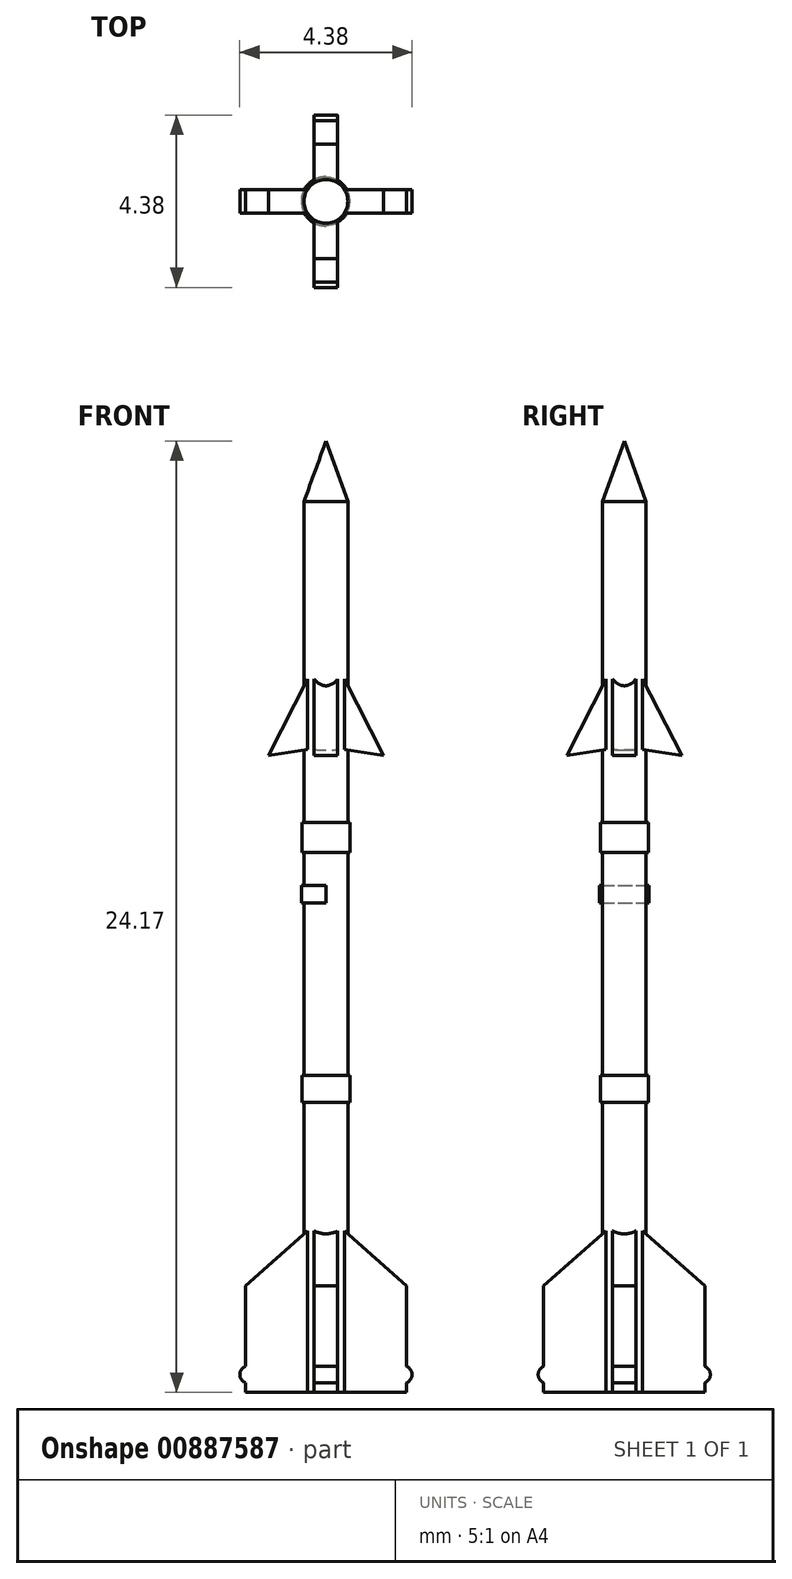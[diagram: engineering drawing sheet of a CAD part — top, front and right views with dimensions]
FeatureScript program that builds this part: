
annotation { "Feature Type Name" : "Feature", "Feature Type Description" : "" }
export const myFeature = defineFeature(function(context is Context, id is Id, definition is map)
    precondition{}
    {
        {
            var Q0;
            Q0=qCreatedBy(makeId("Front.planeOp"),FACE);
            var sketch = newSketch(context, id + "F0", { "sketchPlane" : qUnion([Q0])});
            skLineSegment(sketch, "E0", {"start": v(0, 0) * mm, "end": v(0.56, 0) * mm});
            skLineSegment(sketch, "E1", {"start": v(0.56, 0) * mm, "end": v(0.56, 7.36) * mm});
            skLineSegment(sketch, "E2", {"start": v(0.56, 7.36) * mm, "end": v(0.6, 7.36) * mm});
            skLineSegment(sketch, "E3", {"start": v(0.6, 7.36) * mm, "end": v(0.6, 8.06) * mm});
            skLineSegment(sketch, "E4", {"start": v(0.6, 8.06) * mm, "end": v(0.56, 8.06) * mm});
            skLineSegment(sketch, "E5", {"start": v(0.56, 8.06) * mm, "end": v(0.56, 13.72) * mm});
            skLineSegment(sketch, "E6", {"start": v(0, 24.17) * mm, "end": v(0, 0) * mm});
            skLineSegment(sketch, "E7", {"start": v(0, 24.17) * mm, "end": v(0.56, 22.64) * mm});
            skLineSegment(sketch, "E8.bottom", {"start": v(0.56, 14.48) * mm, "end": v(0.6, 14.48) * mm});
            skLineSegment(sketch, "E8.top", {"start": v(0.56, 13.72) * mm, "end": v(0.6, 13.72) * mm});
            skLineSegment(sketch, "E8.right", {"start": v(0.6, 14.48) * mm, "end": v(0.6, 13.72) * mm});
            skLineSegment(sketch, "E9.trimOffspring", {"start": v(0.56, 14.48) * mm, "end": v(0.56, 22.64) * mm});
            skSolve(sketch);
        }
        {
            var Q0;
            Q0=qSketchRegion(id+"F0",true);
            var Q1;
            Q1=sQuery(id+"F0.wireOp",EDGE,"E6");
            revolve(context, id + "F1", {"surfaceOperationType" : NewSurfaceOperationType.NEW, "entities" : qUnion([Q0]), "axis" : qUnion([Q1]), "revolveType" : RevolveType.FULL});
        }
        {
            var Q0;
            Q0=qCreatedBy(makeId("Front.planeOp"),FACE);
            var sketch = newSketch(context, id + "F2", { "sketchPlane" : qUnion([Q0])});
            skLineSegment(sketch, "E10", {"start": v(2.05, 0) * mm, "end": v(0, 0) * mm});
            skLineSegment(sketch, "E11", {"start": v(2.05, 0) * mm, "end": v(2.05, 0.24) * mm});
            skLineSegment(sketch, "E12", {"start": v(2.05, 2.7) * mm, "end": v(0.4, 4.17) * mm});
            skLineSegment(sketch, "E13", {"start": v(0.4, 4.17) * mm, "end": v(0.4, 16.34) * mm});
            skLineSegment(sketch, "E14", {"start": v(0.4, 16.34) * mm, "end": v(1.46, 16.18) * mm});
            skLineSegment(sketch, "E15", {"start": v(1.46, 16.18) * mm, "end": v(0, 19.04) * mm});
            skLineSegment(sketch, "E16", {"start": v(0, 19.04) * mm, "end": v(0, 0) * mm});
            skLineSegment(sketch, "E17", {"start": v(0.56, 22.64) * mm, "end": v(0.56, -0.42) * mm, "construction": true});
            skPoint(sketch, "E18", {"position": v(0.56, 4.03) * mm});
            skPoint(sketch, "E19", {"position": v(0.56, 16.32) * mm});
            skPoint(sketch, "E20", {"position": v(0.56, 17.95) * mm});
            skArc(sketch, "E21", {"start": v(2.05, 0.24) * mm, "mid": v(2.19, 0.45) * mm, "end": v(2.05, 0.66) * mm});
            skLineSegment(sketch, "E22.trimOffspring", {"start": v(2.05, 0.66) * mm, "end": v(2.05, 2.7) * mm});
            skLineSegment(sketch, "E23.0", {"start": v(-0.56, 22.64) * mm, "end": v(0.56, 22.64) * mm});
            skSolve(sketch);
        }
        {
            var Q0;
            Q0=qSketchRegion(id+"F2",true);
            extrude(context, id + "F3", {"entities" : qUnion([Q0]), "operationType" : NewBodyOperationType.ADD, "depth" : .6 * mm, "offsetDistance" : 25 * mm, "symmetric" : true});
        }
        {
            var Q0;
            Q0=makeQuery(id+"F1.opRevolve","SWEPT_BODY",BODY,{"disambiguationData":[OSD([sQuery(id+"F0.wireOp",EDGE,"E0"),sQuery(id+"F0.wireOp",EDGE,"E1"),sQuery(id+"F0.wireOp",EDGE,"E2"),sQuery(id+"F0.wireOp",EDGE,"E3"),sQuery(id+"F0.wireOp",EDGE,"E4"),sQuery(id+"F0.wireOp",EDGE,"E5"),sQuery(id+"F0.wireOp",EDGE,"E6"),sQuery(id+"F0.wireOp",EDGE,"3DkYhRo3-WWg3-hx7e-zHoR-22PYPzyeQcpA")])]});
            var Q1;
            Q1=makeQuery(id+"F1.opRevolve","SWEPT_FACE",FACE,{"disambiguationData":[OSD([sQuery(id+"F0.wireOp",EDGE,"E5")])]});
            circularPattern(context, id + "F4", {"operationType" : NewBodyOperationType.ADD, "entities" : qUnion([Q0]), "axis" : qUnion([Q1]), "angle" : 360 * degree, "instanceCount" : 4, "equalSpace" : true, "computeTransformsWithoutBuiltin" : true});
        }
        {
            var Q0;
            Q0=qCreatedBy(makeId("Front.planeOp"),FACE);
            var sketch = newSketch(context, id + "F5", { "sketchPlane" : qUnion([Q0])});
            skLineSegment(sketch, "E24.bottom", {"start": v(0, 12.43) * mm, "end": v(-0.63, 12.43) * mm});
            skLineSegment(sketch, "E24.top", {"start": v(0, 12.88) * mm, "end": v(-0.63, 12.88) * mm});
            skLineSegment(sketch, "E24.left", {"start": v(0, 12.43) * mm, "end": v(0, 12.88) * mm});
            skLineSegment(sketch, "E24.right", {"start": v(-0.63, 12.43) * mm, "end": v(-0.63, 12.88) * mm});
            skSolve(sketch);
        }
        {
            var Q0;
            Q0=qSketchRegion(id+"F5",true);
            var Q1;
            Q1=makeQuery(id+"F1.opRevolve","SWEPT_FACE",FACE,{"disambiguationData":[OSD([sQuery(id+"F0.wireOp",EDGE,"E5")])]});
            revolve(context, id + "F6", {"operationType" : NewBodyOperationType.ADD, "surfaceOperationType" : NewSurfaceOperationType.NEW, "entities" : qUnion([Q0]), "axis" : qUnion([Q1]), "revolveType" : RevolveType.SYMMETRIC, "angle" : 180 * degree});
        }
    });
